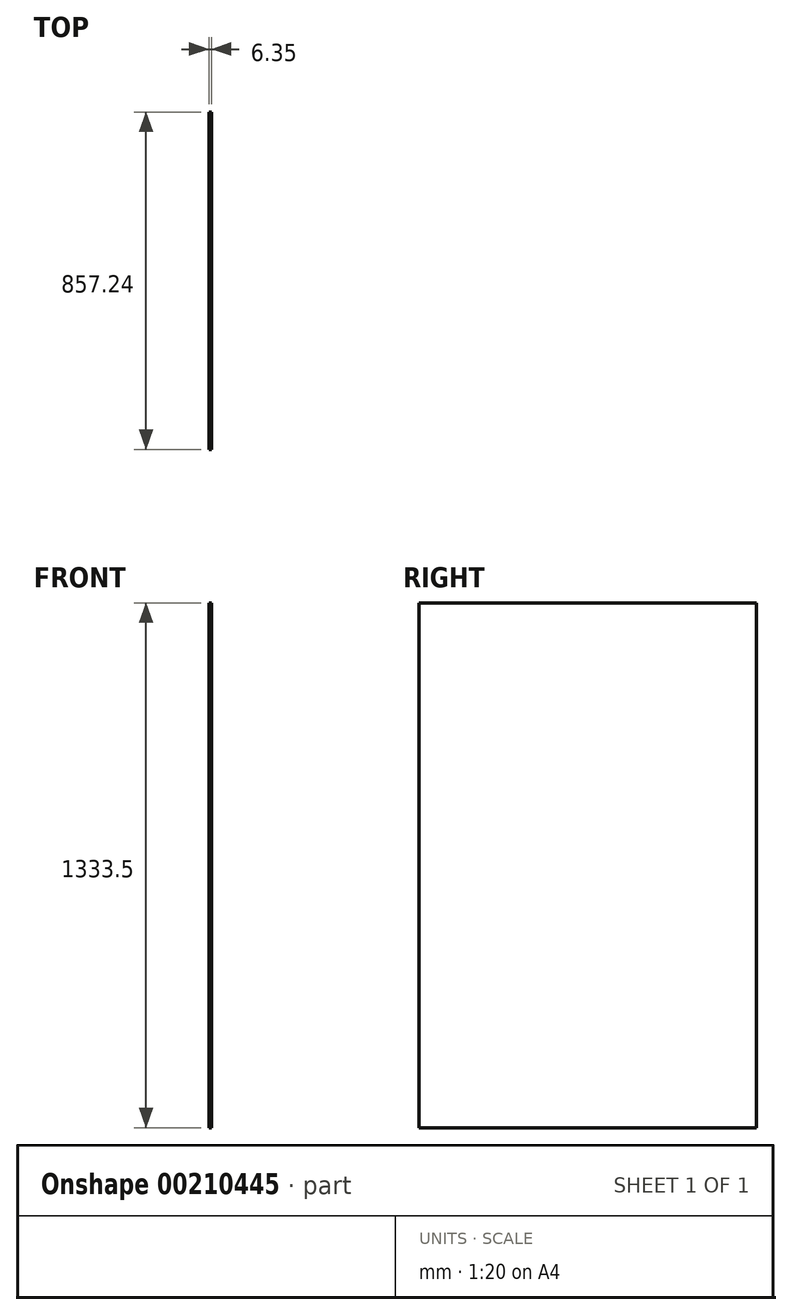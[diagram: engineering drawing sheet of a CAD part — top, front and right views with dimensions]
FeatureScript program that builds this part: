
annotation { "Feature Type Name" : "Feature", "Feature Type Description" : "" }
export const myFeature = defineFeature(function(context is Context, id is Id, definition is map)
    precondition{}
    {
        {
            var Q0;
            Q0=qCreatedBy(makeId("Right.planeOp"),FACE);
            var sketch = newSketch(context, id + "F0", { "sketchPlane" : qUnion([Q0])});
            skLineSegment(sketch, "E0.bottom", {"start": v(428.63, 666.75) * mm, "end": v(-428.62, 666.75) * mm});
            skLineSegment(sketch, "E0.top", {"start": v(428.63, -666.75) * mm, "end": v(-428.63, -666.75) * mm});
            skLineSegment(sketch, "E0.left", {"start": v(428.63, 666.75) * mm, "end": v(428.63, -666.75) * mm});
            skLineSegment(sketch, "E0.right", {"start": v(-428.62, 666.75) * mm, "end": v(-428.63, -666.75) * mm});
            skPoint(sketch, "E0.middle", {"position": v(0, 0) * mm});
            skSolve(sketch);
        }
        {
            var Q0;
            Q0 = qSketchRegion(id + "F0", true);
            extrude(context, id + "F1", {"entities" : qUnion([Q0]), "depth" : 6.35 * mm});
        }
    });
